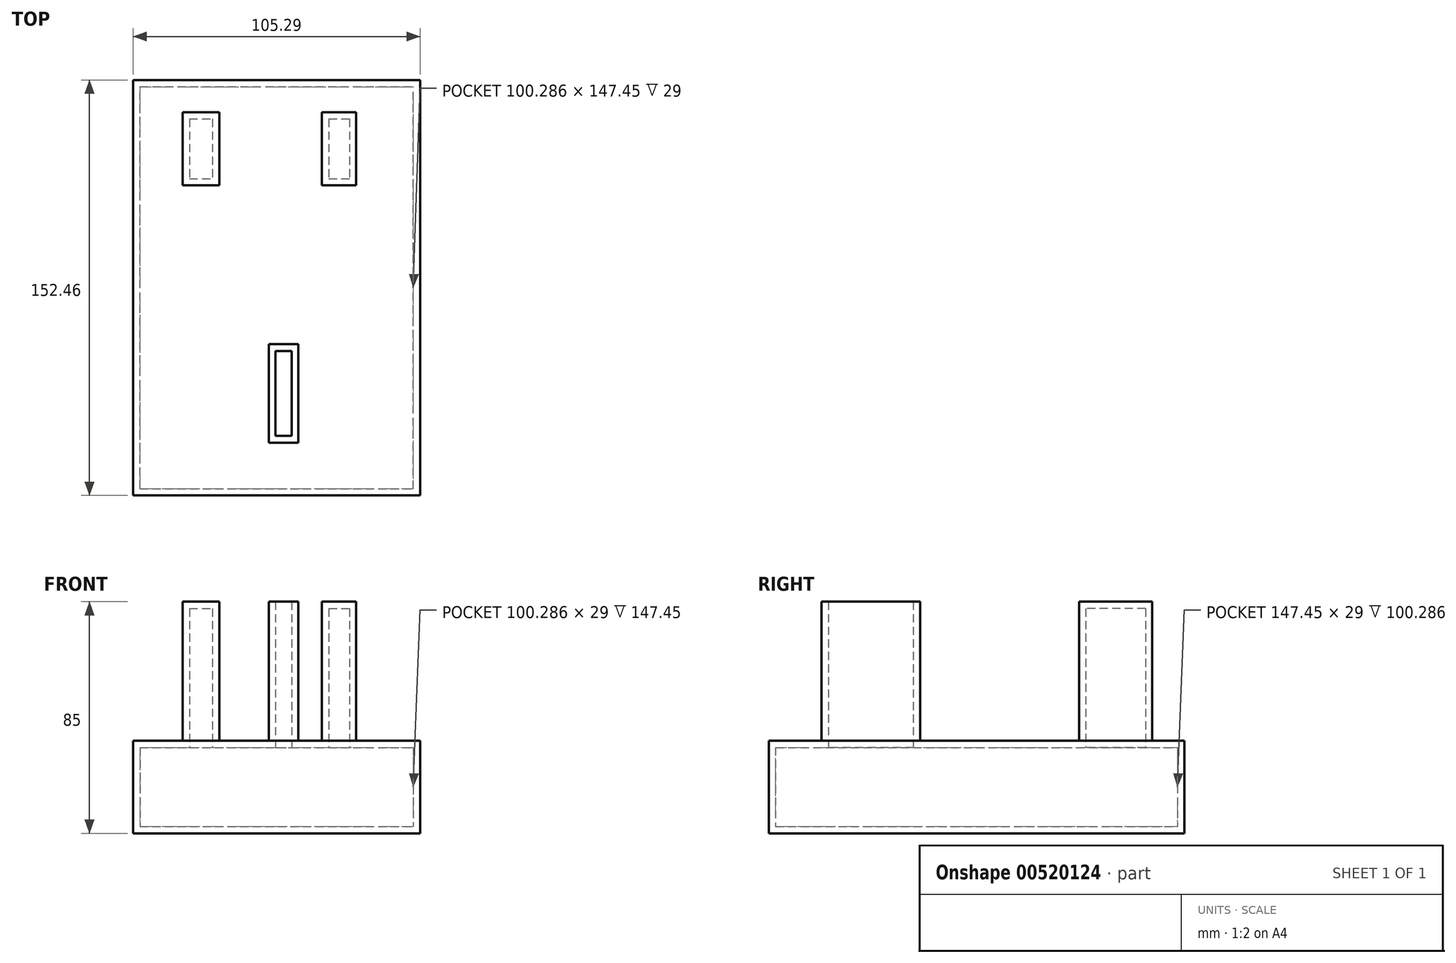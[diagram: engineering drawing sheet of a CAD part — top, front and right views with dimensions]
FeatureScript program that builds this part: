
annotation { "Feature Type Name" : "Feature", "Feature Type Description" : "" }
export const myFeature = defineFeature(function(context is Context, id is Id, definition is map)
    precondition{}
    {
        {
            var Q0;
            Q0=qCreatedBy(makeId("Top.planeOp"),FACE);
            var sketch = newSketch(context, id + "F0", { "sketchPlane" : qUnion([Q0])});
            skLineSegment(sketch, "E0.bottom", {"start": v(-18.17, -42.58) * mm, "end": v(87.12, -42.58) * mm});
            skLineSegment(sketch, "E0.top", {"start": v(-18.17, 109.88) * mm, "end": v(87.12, 109.88) * mm});
            skLineSegment(sketch, "E0.left", {"start": v(-18.17, -42.58) * mm, "end": v(-18.17, 109.88) * mm});
            skLineSegment(sketch, "E0.right", {"start": v(87.12, -42.58) * mm, "end": v(87.12, 109.88) * mm});
            skSolve(sketch);
        }
        {
            var Q0;
            Q0 = qSketchRegion(id + "F0", true);
            extrude(context, id + "F1", {"entities" : qUnion([Q0]), "depth" : 34 * mm, "offsetDistance" : 25 * mm});
        }
        {
            var Q0;
            Q0=makeQuery(id+"F1.opExtrude","CAP_FACE",FACE,{"disambiguationData":[OSD([sQuery(id+"F0.wireOp",EDGE,"E0.bottom"),sQuery(id+"F0.wireOp",EDGE,"E0.top"),sQuery(id+"F0.wireOp",EDGE,"E0.left"),sQuery(id+"F0.wireOp",EDGE,"E0.right")])],"isStart":false});
            var sketch = newSketch(context, id + "F2", { "sketchPlane" : qUnion([Q0])});
            skLineSegment(sketch, "E1.bottom", {"start": v(0, 98.09) * mm, "end": v(13.39, 98.09) * mm});
            skLineSegment(sketch, "E1.top", {"start": v(0, 71.2) * mm, "end": v(13.39, 71.2) * mm});
            skLineSegment(sketch, "E1.left", {"start": v(0, 98.09) * mm, "end": v(0, 71.2) * mm});
            skLineSegment(sketch, "E1.right", {"start": v(13.39, 98.09) * mm, "end": v(13.39, 71.2) * mm});
            skLineSegment(sketch, "E2.bottom", {"start": v(51.1, 98.09) * mm, "end": v(63.66, 98.09) * mm});
            skLineSegment(sketch, "E2.top", {"start": v(51.1, 71.2) * mm, "end": v(63.66, 71.2) * mm});
            skLineSegment(sketch, "E2.left", {"start": v(51.1, 98.09) * mm, "end": v(51.1, 71.2) * mm});
            skLineSegment(sketch, "E2.right", {"start": v(63.66, 98.09) * mm, "end": v(63.66, 71.2) * mm});
            skLineSegment(sketch, "E3.bottom", {"start": v(31.58, 12.95) * mm, "end": v(42.45, 12.95) * mm});
            skLineSegment(sketch, "E3.top", {"start": v(31.58, -23.23) * mm, "end": v(42.45, -23.23) * mm});
            skLineSegment(sketch, "E3.left", {"start": v(31.58, 12.95) * mm, "end": v(31.58, -23.23) * mm});
            skLineSegment(sketch, "E3.right", {"start": v(42.45, 12.95) * mm, "end": v(42.45, -23.23) * mm});
            skSolve(sketch);
        }
        {
            var Q0;
            Q0 = qSketchRegion(id + "F2", true);
            extrude(context, id + "F3", {"entities" : qUnion([Q0]), "operationType" : NewBodyOperationType.ADD, "depth" : 51 * mm, "offsetDistance" : 25 * mm});
        }
        {
            var Q0;
            Q0=makeQuery(id+"F3.opExtrude","CAP_FACE",FACE,{"disambiguationData":[OSD([sQuery(id+"F2.wireOp",EDGE,"E3.bottom"),sQuery(id+"F2.wireOp",EDGE,"E3.top"),sQuery(id+"F2.wireOp",EDGE,"E3.left"),sQuery(id+"F2.wireOp",EDGE,"E3.right")])],"isStart":false});
            shell(context, id + "F4", {"entities" : qUnion([Q0]), "thickness" : 2.5 * mm});
        }
    });
